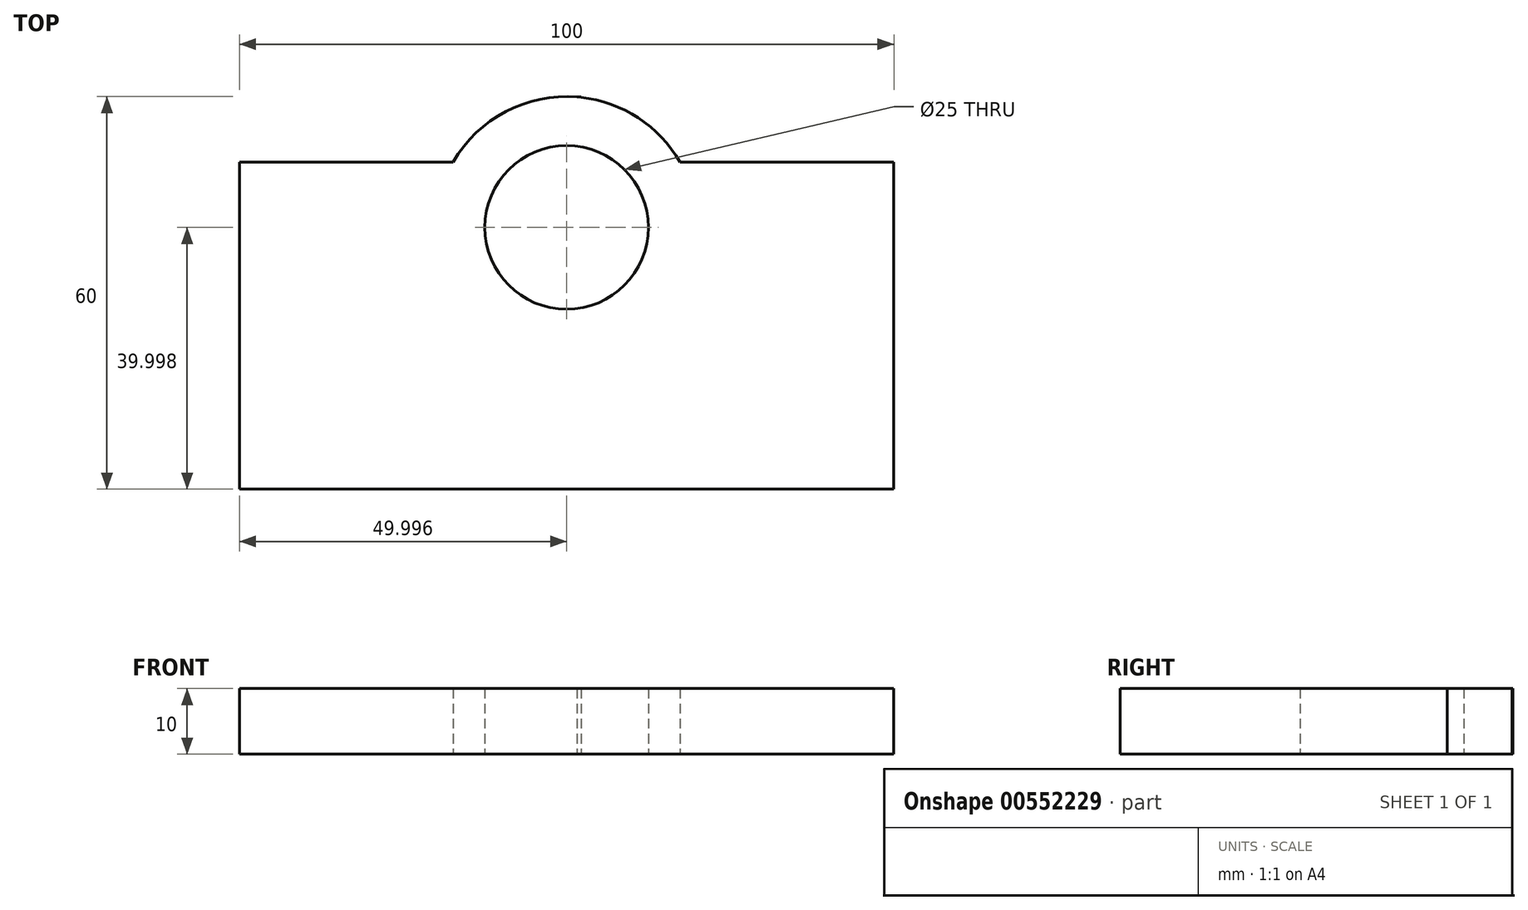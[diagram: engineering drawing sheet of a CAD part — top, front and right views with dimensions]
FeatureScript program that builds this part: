
annotation { "Feature Type Name" : "Feature", "Feature Type Description" : "" }
export const myFeature = defineFeature(function(context is Context, id is Id, definition is map)
    precondition{}
    {
        {
            var Q0;
            Q0=qCreatedBy(makeId("Top.planeOp"),FACE);
            var sketch = newSketch(context, id + "F0", { "sketchPlane" : qUnion([Q0])});
            skLineSegment(sketch, "E0.bottom", {"start": v(-53.21, 28.04) * mm, "end": v(46.79, 28.04) * mm});
            skLineSegment(sketch, "E0.top", {"start": v(-53.21, -21.96) * mm, "end": v(46.79, -21.96) * mm});
            skLineSegment(sketch, "E0.left", {"start": v(-53.21, 28.04) * mm, "end": v(-53.21, -21.96) * mm});
            skLineSegment(sketch, "E0.right", {"start": v(46.79, 28.04) * mm, "end": v(46.79, -21.96) * mm});
            skCircle(sketch, "E1", {"center": v(-3.21, 18.04) * mm, "radius": 20 * mm});
            skCircle(sketch, "E2", {"center": v(-3.21, 18.04) * mm, "radius": 12.5 * mm});
            skLineSegment(sketch, "E3.bottom", {"start": v(-4.81, 37.97) * mm, "end": v(-1.02, 37.97) * mm});
            skLineSegment(sketch, "E3.top", {"start": v(-4.81, 30.34) * mm, "end": v(-1.02, 30.34) * mm});
            skLineSegment(sketch, "E3.left", {"start": v(-4.81, 37.97) * mm, "end": v(-4.81, 30.34) * mm});
            skLineSegment(sketch, "E3.right", {"start": v(-1.02, 37.97) * mm, "end": v(-1.02, 30.34) * mm});
            skSolve(sketch);
        }
        {
            var Q0;
            Q0 = qSketchRegion(id + "F0", true);
            extrude(context, id + "F1", {"entities" : qUnion([Q0]), "endBound" : BoundingType.SYMMETRIC, "depth" : 10 * mm, "offsetDistance" : 25 * mm});
        }
    });
